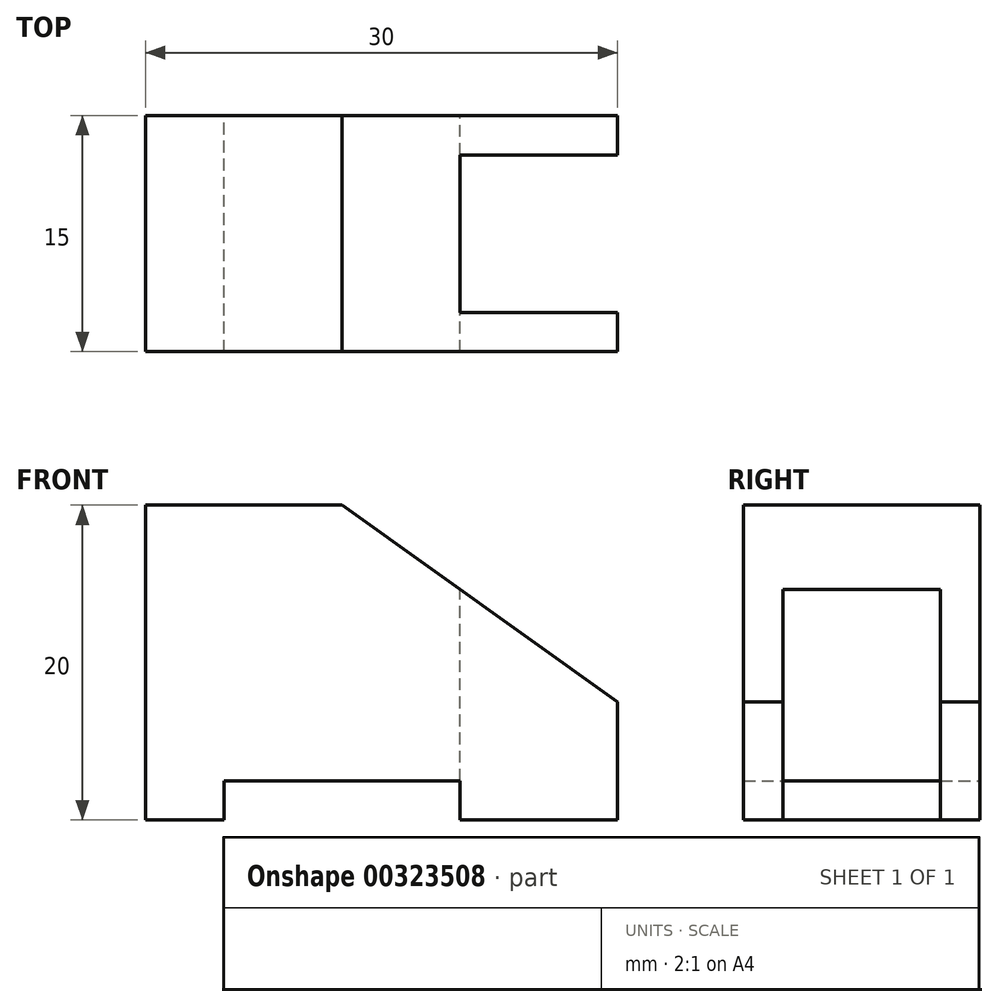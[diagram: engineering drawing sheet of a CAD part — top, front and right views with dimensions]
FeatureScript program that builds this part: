
annotation { "Feature Type Name" : "Feature", "Feature Type Description" : "" }
export const myFeature = defineFeature(function(context is Context, id is Id, definition is map)
    precondition{}
    {
        {
            var Q0;
            Q0=qCreatedBy(makeId("Front.planeOp"),FACE);
            var sketch = newSketch(context, id + "F0", { "sketchPlane" : qUnion([Q0])});
            skLineSegment(sketch, "E0.bottom", {"start": v(-15, 20) * mm, "end": v(-2.5, 20) * mm});
            skLineSegment(sketch, "E0.top", {"start": v(-15, 0) * mm, "end": v(-10, 0) * mm});
            skLineSegment(sketch, "E0.left", {"start": v(-15, 20) * mm, "end": v(-15, 0) * mm});
            skLineSegment(sketch, "E0.right", {"start": v(15, 7.5) * mm, "end": v(15, 0) * mm});
            skLineSegment(sketch, "E1.top", {"start": v(-10, 2.5) * mm, "end": v(5, 2.5) * mm});
            skLineSegment(sketch, "E1.left", {"start": v(-10, 0) * mm, "end": v(-10, 2.5) * mm});
            skLineSegment(sketch, "E1.right", {"start": v(5, 0) * mm, "end": v(5, 2.5) * mm});
            skLineSegment(sketch, "E2.trimOffspring", {"start": v(5, 0) * mm, "end": v(15, 0) * mm});
            skLineSegment(sketch, "E3", {"start": v(0, -9.7) * mm, "end": v(0, 31.27) * mm, "construction": true});
            skLineSegment(sketch, "E4", {"start": v(15, 7.5) * mm, "end": v(-2.5, 20) * mm});
            skSolve(sketch);
        }
        {
            var Q0;
            Q0 = qSketchRegion(id + "F0", true);
            extrude(context, id + "F1", {"entities" : qUnion([Q0]), "endBound" : BoundingType.SYMMETRIC, "depth" : 15 * mm});
        }
        {
            var Q0;
            Q0=qCreatedBy(makeId("Front.planeOp"),FACE);
            var sketch = newSketch(context, id + "F2", { "sketchPlane" : qUnion([Q0])});
            skLineSegment(sketch, "E5.0.0", {"start": v(5, 2.5) * mm, "end": v(5, 0) * mm});
            skLineSegment(sketch, "E5.0.1", {"start": v(5, 0) * mm, "end": v(15, 0) * mm});
            skLineSegment(sketch, "E5.0.2", {"start": v(15, 0) * mm, "end": v(15, 7.5) * mm});
            skLineSegment(sketch, "E5.0.3", {"start": v(15, 7.5) * mm, "end": v(5, 14.64) * mm});
            skLineSegment(sketch, "E6", {"start": v(5, 0) * mm, "end": v(5, 14.64) * mm});
            skLineSegment(sketch, "E7", {"start": v(5, 14.64) * mm, "end": v(15, 7.5) * mm});
            skLineSegment(sketch, "E8", {"start": v(15, 0) * mm, "end": v(5, 0) * mm});
            skPoint(sketch, "E5.0.7.end.orphan", {"position": v(-10, 2.5) * mm});
            skPoint(sketch, "E5.0.6.end.orphan", {"position": v(-10, 0) * mm});
            skPoint(sketch, "E5.0.5.end.orphan", {"position": v(-15, 0) * mm});
            skPoint(sketch, "E5.0.4.end.orphan", {"position": v(-15, 20) * mm});
            skPoint(sketch, "E9.orphan", {"position": v(-2.5, 20) * mm});
            skSolve(sketch);
        }
        {
            var Q0;
            Q0 = qSketchRegion(id + "F2", true);
            extrude(context, id + "F3", {"entities" : qUnion([Q0]), "operationType" : NewBodyOperationType.REMOVE, "endBound" : BoundingType.SYMMETRIC, "oppositeDirection" : true, "depth" : 10 * mm});
        }
    });
